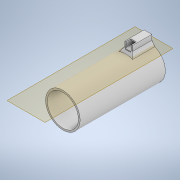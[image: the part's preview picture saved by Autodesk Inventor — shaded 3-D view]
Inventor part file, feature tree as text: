
AUTODESK INVENTOR PART (.ipt)
format: ipt  version: 2021 (Build 250183000, 183)  size: 797,696 bytes
history: native  units: in
note: dims shown in document units (in); Inventor stores cm internally (conversion verified against a paired STEP export)
features: projected_geometry x11, extrude x9, sketch x8, chamfer x5, plane x1, pattern_linear x1, fillet x1
ambient origin geometry x8: Origin, YZ Plane, XZ Plane, XY Plane, X Axis, Y Axis, Z Axis, Center Point
bodies: Solid1 (feature_tree)
feature tree (36):
  extrude  "Extrusion1"  Depth=4.3307in TaperAngle=0.0deg
  plane  "Work Plane1"
  extrude  "Extrusion7"  Depth=4.252in TaperAngle=0.0deg
  extrude  "Extrusion8"  Depth=0.3937in
  extrude  "Extrusion9"  Depth=0.3937in
  extrude  "Extrusion10"  Depth=0.1181in
  extrude  "Extrusion11"  Depth=0.0591in
  extrude  "Extrusion12"  Depth=0.0591in
  pattern_linear  "Rectangular Pattern3"  Spacing1=1.6929in  [1 undecoded]
  extrude  "Extrusion13"  Depth=0.0394in
  chamfer  "Chamfer2"  Distance=0.0394in
  chamfer  "Chamfer3"  Distance=0.0098in
  chamfer  "Chamfer4"  Distance=8.2677in
  chamfer  "Chamfer5"  Distance=0.248in
  extrude  "Extrusion14"  Depth=0.3937in TaperAngle=0.0deg
  chamfer  "Chamfer6"  Distance=0.0787in
  fillet  "Fillet10"  Radius=0.0059in
  sketch  "Sketch2"  dims[d2=1.752in d3=4.3307in d4=0.0in]
  sketch  "Sketch9"  dims[d54=1.5748in d55=4.252in d56=0.0in]
  projected_geometry  "Projected Loop7"
  sketch  "Sketch10"  dims[d57=0.3937in d58=0.9843in]
  projected_geometry  "Projected Loop8"
  sketch  "Sketch11"  dims[d59=0.3937in d60=0.0236in d61=0.0in d62=0.0in d63=0.1929in]
  projected_geometry  "Projected Loop9"
  sketch  "Sketch12"  dims[d64=0.122in d65=0.1181in]
  projected_geometry  "Projected Loop10"
  projected_geometry  "Projected Loop11"
  projected_geometry  "Projected Loop12"
  sketch  "Sketch14"  dims[d66=0.0551in d67=0.0in d68=0.0591in]
  projected_geometry  "Projected Loop14"
  projected_geometry  "Projected Loop15"
  sketch  "Sketch16"  dims[d69=0.0591in d70=0.0591in]
  projected_geometry  "Projected Loop16"
  sketch  "Sketch17"  dims[d71=0.935in d72=0.0in d76=1.6929in d77=0.0in d84=1.811in d85=0.0394in d86=0.0098in d87=0.0in d88=8.2677in d90=0.0787in d92=0.248in d93=0.3937in d94=0.0in d95=0.0787in d96=0.0059in d97=0.0157in d98=0.0787in d99=45.0deg d100=0.0118in d101=0.0787in d102=45.0deg d103=0.1575in d104=0.0787in d105=45.0deg d106=0.0098in d107=0.0787in d108=45.0deg d109=0.5906in d110=0.0433in d111=0.0in d112=0.0433in d113=0.0787in d114=45.0deg d115=0.0394in d19=0.0197in d20=0.0344in d21=0.0197in d22=0.0344in]
  projected_geometry  "Projected Loop17"
  projected_geometry  "Projected Loop18"
note: 1 required parameter value undecoded (feature->parameter linkage not recoverable at this tier; creation-order binding heuristic only, values carry confidence <= 0.55)
